# Revit family: Multibrand_Prosys_R0090_BIM_DE
name_source: partatom
category: Plumbing Fixtures
revit_build: Autodesk Revit 2017 (Build: 20171027_0315(x64)
units: mm (PartAtom-declared; Revit-internal decimal feet)

## family parameters
Cut with Voids When Loaded = No
Host = Face
OmniClass Number = 23.45.05.21.11.11
OmniClass Title = Water Operated Water Closets
Part Type = Normal
Room Calculation Point = No
Round Connector Dimension = Use Diameter
Shared = Yes

## types (1)
- R009067 - 820 Full frame Dry mechanical WC  CL1
    Accessories = www.idealspec.de
    AreaUnits = millimeters
    Assembly Code = C1030200
    AssetType = Fixed
    BIMObjectName = IS_IdealStandard_WC cistern fittings_Prosys_S0090
    BREEAMApproved = No
    Brand = Ideal Standrad
    CWFU = 0
    ConnectionType = Plumbing
    Cost = 0 $
    Default Elevation = 0 mm  [stored 0 ft]
    Description = Prosys 150M-Rahmen, wandmontierte WC-Schalen, max. Belastung 400 kg, für feste oder leichte Wände min
    DurationUnit = year
    ECA = No
    Features = Prosys 150 m Rahmen für wandmontierte WC-Becken, Intalation auf Massivholz oder zwischen leichten Gipskartonplatten Paneel 150 mm min.
    Finish = Metal
    HWFU = 0
    Help = https://www.idealstandard.de
    IfcExportAs = IfcSanitaryTerminalType
    IfcExportType = CISTERN
    InstallationInstructions = https://www.idealstandard.de
    LinearUnits = millimeters
    Manufacturer = https://www.idealstandard.de
    ManufacturerURL = https://www.idealstandard.de
    Model = R009067
    ModelNumber = R009067
    ModelReference = Prosys 150M-Rahmen, wandmontierte WC-Schalen, max. Belastung 400 kg, für feste oder leichte Wände min
    NBSDescription = WC cistern fittings
    NBSReference = 45-30-70/387
    Name = WCCisternFittings_Prossys_R0090_IdealStandard
    NettWeight = 9.4Kg
    NominalDepth = 150 mm
    NominalHeight = 715 mm  [stored 2.3458 ft]
    NominalLength = 751 mm  [stored 2.46391 ft]
    NominalWidth = 400 mm  [stored 1.31234 ft]
    ProductInformation = https://www.idealstandard.de
    Shape = Regtangular
    Size = 400 x 150 x 754 mm
    Space = Internal
    SpilloverLevel = 0 mm  [stored 0 ft]
    ToiletPanType = WashDown
    ToiletType = Other
    URL = www.idealspec.de
    Uniclass2 = Pr_40_20_93_89
    Uniclass2015Code = Pr_40_20_93
    Uniclass2015Description = Urinal and WC fittings
    Uniclass2015Title = Urinal and WC fittings
    Uniclass2015Version = Products v1.1
    Version = 1
    VolumeUnits = Litres
    WFU = 0
    WRAS = No
    WarrantyDescription = Manufacturers Warranty
    WarrantyDurationUnit = year
    WarrantyGuarantorParts = https://www.idealstandard.de
    WaterEfficientProduct = No

note: [stored X ft] marks values corroborated as IEEE doubles in the binary element streams (Revit-internal decimal feet)

## geometry (parser evidence)
native form markers: Sweep x7
no freeform markers — native parametric forms only
